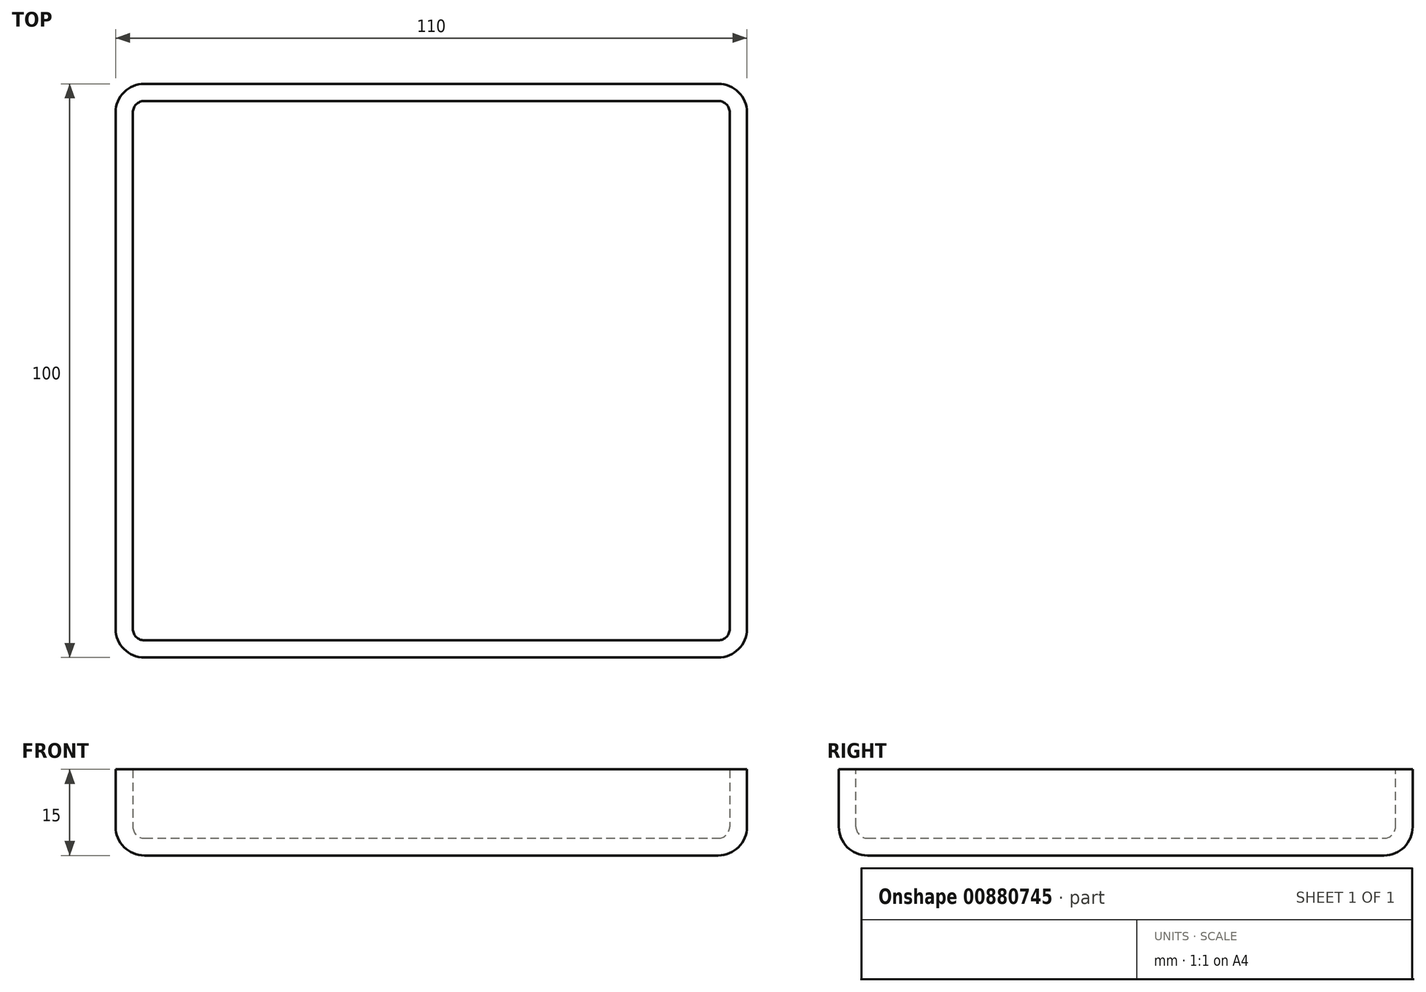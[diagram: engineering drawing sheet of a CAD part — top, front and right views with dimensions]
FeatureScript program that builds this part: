
annotation { "Feature Type Name" : "Feature", "Feature Type Description" : "" }
export const myFeature = defineFeature(function(context is Context, id is Id, definition is map)
    precondition{}
    {
        {
            var Q0;
            Q0=qCreatedBy(makeId("Top.planeOp"),FACE);
            var sketch = newSketch(context, id + "F0", { "sketchPlane" : qUnion([Q0])});
            skLineSegment(sketch, "E0.bottom", {"start": v(-110, 100) * mm, "end": v(0, 100) * mm});
            skLineSegment(sketch, "E0.top", {"start": v(-110, 0) * mm, "end": v(0, 0) * mm});
            skLineSegment(sketch, "E0.left", {"start": v(-110, 100) * mm, "end": v(-110, 0) * mm});
            skLineSegment(sketch, "E0.right", {"start": v(0, 100) * mm, "end": v(0, 0) * mm});
            skSolve(sketch);
        }
        {
            var Q0;
            Q0=makeQuery(id+"F0.imprint","IMPRINT",FACE,{"disambiguationData":[TD([[makeQuery(id+"F0.imprint","IMPRINT",EDGE,{"derivedFrom":sQuery(id+"F0.wireOp",EDGE,"E0.bottom")}),-1.0]])]});
            extrude(context, id + "F1", {"entities" : qUnion([Q0]), "depth" : 15 * mm, "offsetDistance" : 25 * mm});
        }
        {
            var Q0;
            Q0=makeQuery(id+"F1.opExtrude","CAP_EDGE",EDGE,{"disambiguationData":[OSD([sQuery(id+"F0.wireOp",EDGE,"E0.top")])],"isStart":true});
            var Q1;
            Q1=makeQuery(id+"F1.opExtrude","CAP_EDGE",EDGE,{"disambiguationData":[OSD([sQuery(id+"F0.wireOp",EDGE,"E0.right")])],"isStart":true});
            var Q2;
            Q2=makeQuery(id+"F1.opExtrude","CAP_EDGE",EDGE,{"disambiguationData":[OSD([sQuery(id+"F0.wireOp",EDGE,"E0.bottom")])],"isStart":true});
            var Q3;
            Q3=makeQuery(id+"F1.opExtrude","CAP_EDGE",EDGE,{"disambiguationData":[OSD([sQuery(id+"F0.wireOp",EDGE,"E0.left")])],"isStart":true});
            fillet(context, id + "F2", {"entities" : qUnion([Q0, Q1, Q2, Q3]), "radius" : 5 * mm, "tangentPropagation" : true, "allowEdgeOverflow" : false});
        }
        {
            var Q0;
            Q0=makeQuery(id+"F1.opExtrude","SWEPT_EDGE",EDGE,{"disambiguationData":[OSD([sQuery(id+"F0.wireOp",EDGE,"E0.top"),sQuery(id+"F0.wireOp",EDGE,"E0.right")])]});
            var Q1;
            Q1=makeQuery(id+"F1.opExtrude","SWEPT_EDGE",EDGE,{"disambiguationData":[OSD([sQuery(id+"F0.wireOp",EDGE,"E0.top"),sQuery(id+"F0.wireOp",EDGE,"E0.left")])]});
            var Q2;
            Q2=makeQuery(id+"F1.opExtrude","SWEPT_EDGE",EDGE,{"disambiguationData":[OSD([sQuery(id+"F0.wireOp",EDGE,"E0.bottom"),sQuery(id+"F0.wireOp",EDGE,"E0.right")])]});
            var Q3;
            Q3=makeQuery(id+"F1.opExtrude","SWEPT_EDGE",EDGE,{"disambiguationData":[OSD([sQuery(id+"F0.wireOp",EDGE,"E0.bottom"),sQuery(id+"F0.wireOp",EDGE,"E0.left")])]});
            fillet(context, id + "F3", {"entities" : qUnion([Q0, Q1, Q2, Q3]), "radius" : 5 * mm, "tangentPropagation" : true, "allowEdgeOverflow" : false});
        }
        {
            var Q0;
            Q0=makeQuery(id+"F1.opExtrude","CAP_FACE",FACE,{"disambiguationData":[OSD([sQuery(id+"F0.wireOp",EDGE,"E0.bottom"),sQuery(id+"F0.wireOp",EDGE,"E0.top"),sQuery(id+"F0.wireOp",EDGE,"E0.left"),sQuery(id+"F0.wireOp",EDGE,"E0.right")])],"isStart":false});
            shell(context, id + "F4", {"entities" : qUnion([Q0]), "thickness" : 3 * mm});
        }
    });
